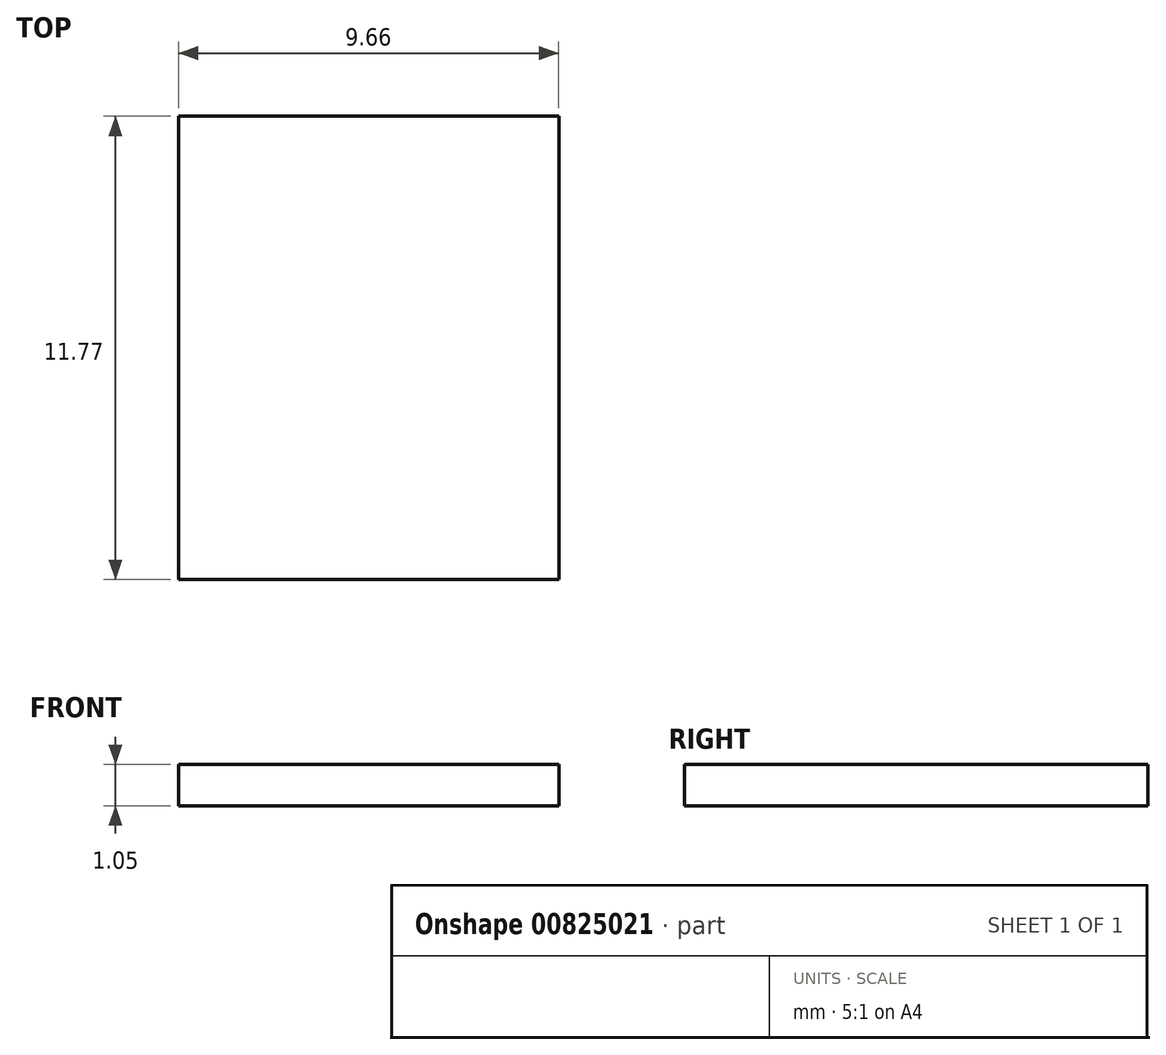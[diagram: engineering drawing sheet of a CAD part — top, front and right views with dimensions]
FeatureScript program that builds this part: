
annotation { "Feature Type Name" : "Feature", "Feature Type Description" : "" }
export const myFeature = defineFeature(function(context is Context, id is Id, definition is map)
    precondition{}
    {
        {
            var Q0;
            Q0=qCreatedBy(makeId("Top.planeOp"),FACE);
            var sketch = newSketch(context, id + "F0", { "sketchPlane" : qUnion([Q0])});
            skLineSegment(sketch, "E0", {"start": v(-31.93, 18.92) * mm, "end": v(-31.93, 7.15) * mm});
            skLineSegment(sketch, "E1", {"start": v(-31.93, 7.15) * mm, "end": v(-22.27, 7.15) * mm});
            skLineSegment(sketch, "E2", {"start": v(-22.27, 7.15) * mm, "end": v(-22.27, 18.92) * mm});
            skLineSegment(sketch, "E3", {"start": v(-22.27, 18.92) * mm, "end": v(-31.93, 18.92) * mm});
            skSolve(sketch);
        }
        {
            var Q0;
            Q0=makeQuery(id+"F0.imprint","IMPRINT",FACE,{"disambiguationData":[TD([[makeQuery(id+"F0.imprint","IMPRINT",EDGE,{"derivedFrom":sQuery(id+"F0.wireOp",EDGE,"E0")}),1.0]])]});
            extrude(context, id + "F1", {"entities" : qUnion([Q0]), "depth" : 1.05 * mm, "offsetDistance" : 25.4 * mm});
        }
    });
